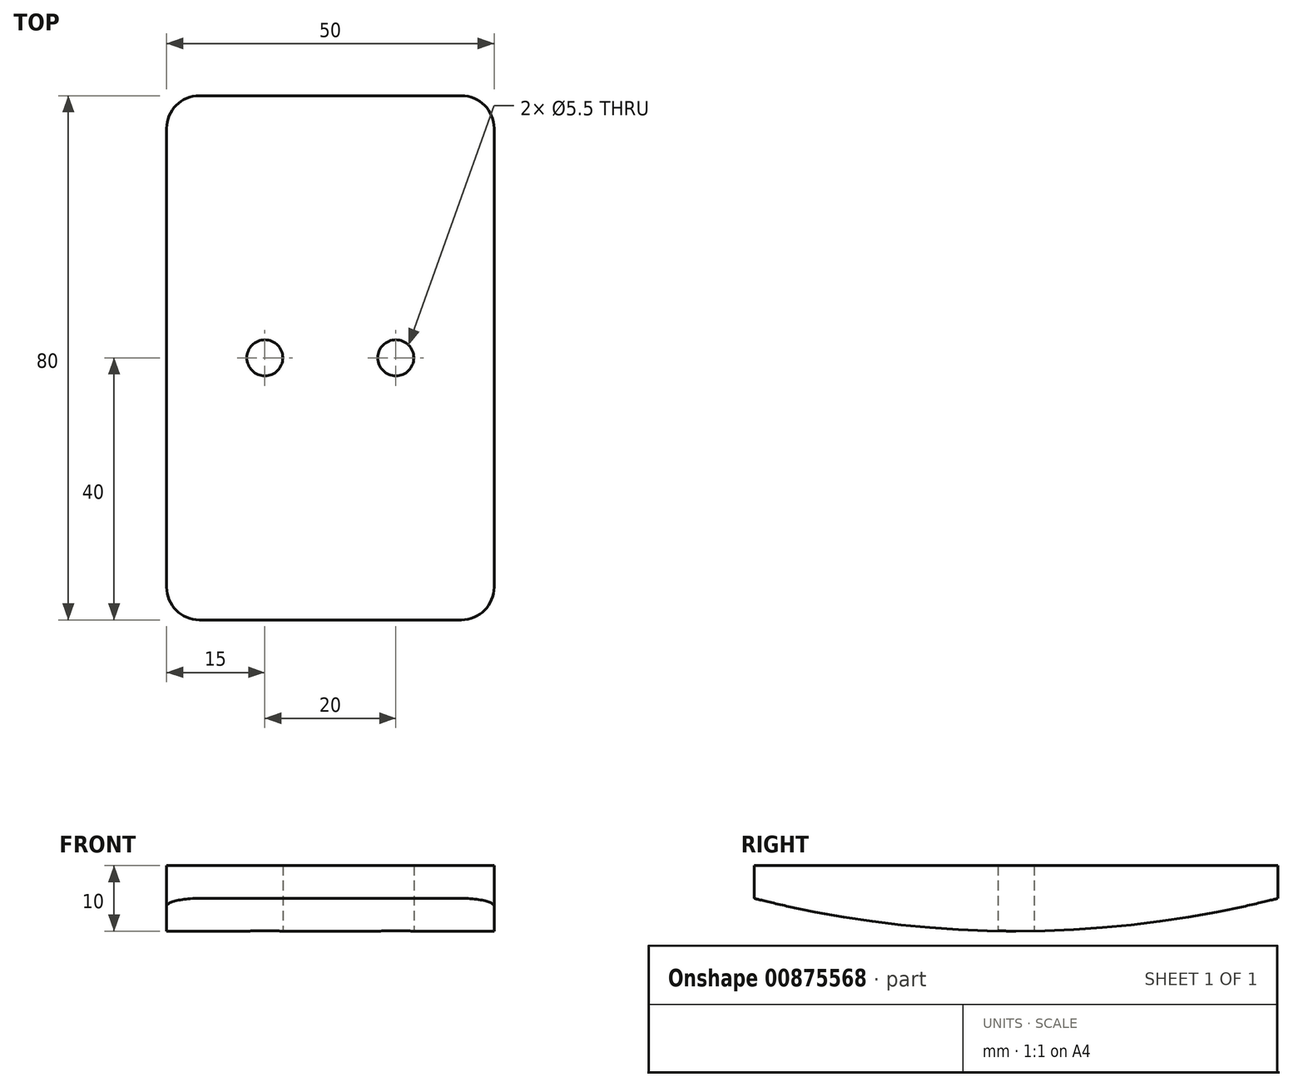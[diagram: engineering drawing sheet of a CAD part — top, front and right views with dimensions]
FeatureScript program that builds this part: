
annotation { "Feature Type Name" : "Feature", "Feature Type Description" : "" }
export const myFeature = defineFeature(function(context is Context, id is Id, definition is map)
    precondition{}
    {
        {
            var Q0;
            Q0=qCreatedBy(makeId("Top.planeOp"),FACE);
            var sketch = newSketch(context, id + "F0", { "sketchPlane" : qUnion([Q0])});
            skLineSegment(sketch, "E0.bottom", {"start": v(-25, 40) * mm, "end": v(25, 40) * mm});
            skLineSegment(sketch, "E0.top", {"start": v(-25, -40) * mm, "end": v(25, -40) * mm});
            skLineSegment(sketch, "E0.left", {"start": v(-25, 40) * mm, "end": v(-25, -40) * mm});
            skLineSegment(sketch, "E0.right", {"start": v(25, 40) * mm, "end": v(25, -40) * mm});
            skPoint(sketch, "E0.middle", {"position": v(0, 0) * mm});
            skCircle(sketch, "E1", {"center": v(-10, 0) * mm, "radius": 2.75 * mm});
            skCircle(sketch, "E2.MirrorC", {"center": v(10, 0) * mm, "radius": 2.75 * mm});
            skSolve(sketch);
        }
        {
            var Q0;
            Q0=makeQuery(id+"F0.imprint","IMPRINT",FACE,{"disambiguationData":[TD([[makeQuery(id+"F0.imprint","IMPRINT",EDGE,{"derivedFrom":sQuery(id+"F0.wireOp",EDGE,"E0.bottom")}),-1.0]])]});
            extrude(context, id + "F1", {"entities" : qUnion([Q0]), "depth" : 10 * mm, "offsetDistance" : 25 * mm});
        }
        {
            var Q0;
            Q0=makeQuery(id+"F1.opExtrude","SWEPT_FACE",FACE,{"disambiguationData":[OSD([sQuery(id+"F0.wireOp",EDGE,"E0.right")])]});
            var sketch = newSketch(context, id + "F2", { "sketchPlane" : qUnion([Q0])});
            skArc(sketch, "E3", {"start": v(-40, 5) * mm, "mid": v(0, 0) * mm, "end": v(40, 5) * mm});
            skSolve(sketch);
        }
        {
            var Q0;
            Q0 = qSketchRegion(id + "F2", true);
            var Q1;
            {var subQ0=sQuery(id+"F2.wireOp",EDGE,"E3");var subQ1=sQuery(id+"F0.wireOp",EDGE,"E0.right");var subQ4=makeQuery(id+"F1.opExtrude","CAP_EDGE",EDGE,{"disambiguationData":[OSD([subQ1])],"isStart":true});var subQ5=makeQuery(id+"F2.imprint","INTERSECT",VERTEX,{"derivedFrom":[subQ4,subQ0]});Q1=makeQuery(id+"F2.imprint","IMPRINT",FACE,{"disambiguationData":[TD([[makeQuery(id+"F2.imprint","IMPRINT",EDGE,{"disambiguationData":[TD([[subQ5,-1.0]])],"derivedFrom":subQ0}),-1.0]])]});}
            var Q2;
            {var subQ0=sQuery(id+"F2.wireOp",EDGE,"E3");var subQ1=sQuery(id+"F0.wireOp",EDGE,"E0.right");var subQ4=makeQuery(id+"F1.opExtrude","CAP_EDGE",EDGE,{"disambiguationData":[OSD([subQ1])],"isStart":true});var subQ5=makeQuery(id+"F2.imprint","INTERSECT",VERTEX,{"derivedFrom":[subQ4,subQ0]});Q2=makeQuery(id+"F2.imprint","IMPRINT",FACE,{"disambiguationData":[TD([[makeQuery(id+"F2.imprint","IMPRINT",EDGE,{"disambiguationData":[TD([[subQ5,1.0]])],"derivedFrom":subQ0}),-1.0]])]});}
            extrude(context, id + "F3", {"entities" : qUnion([Q0, Q1, Q2]), "operationType" : NewBodyOperationType.REMOVE, "endBound" : BoundingType.THROUGH_ALL, "oppositeDirection" : true, "depth" : 25 * mm, "offsetDistance" : 25 * mm});
        }
        {
            var Q0;
            Q0=makeQuery(id+"F1.opExtrude","SWEPT_EDGE",EDGE,{"disambiguationData":[OSD([sQuery(id+"F0.wireOp",EDGE,"E0.top"),sQuery(id+"F0.wireOp",EDGE,"E0.right")])]});
            var Q1;
            Q1=makeQuery(id+"F1.opExtrude","SWEPT_EDGE",EDGE,{"disambiguationData":[OSD([sQuery(id+"F0.wireOp",EDGE,"E0.top"),sQuery(id+"F0.wireOp",EDGE,"E0.left")])]});
            var Q2;
            Q2=makeQuery(id+"F1.opExtrude","SWEPT_EDGE",EDGE,{"disambiguationData":[OSD([sQuery(id+"F0.wireOp",EDGE,"E0.bottom"),sQuery(id+"F0.wireOp",EDGE,"E0.right")])]});
            var Q3;
            Q3=makeQuery(id+"F1.opExtrude","SWEPT_EDGE",EDGE,{"disambiguationData":[OSD([sQuery(id+"F0.wireOp",EDGE,"E0.bottom"),sQuery(id+"F0.wireOp",EDGE,"E0.left")])]});
            fillet(context, id + "F4", {"entities" : qUnion([Q0, Q1, Q2, Q3]), "radius" : 5 * mm, "tangentPropagation" : true, "allowEdgeOverflow" : false});
        }
    });
